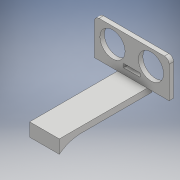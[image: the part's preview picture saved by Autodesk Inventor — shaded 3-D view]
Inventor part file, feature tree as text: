
AUTODESK INVENTOR PART (.ipt)
format: ipt  version: 2018 (Build 220112000, 112)  size: 144,384 bytes
history: native  units: mm
features: reference x3, other x3, extrude x2, sketch x2, projected_geometry x1
ambient origin geometry x8: Origin, YZ Plane, XZ Plane, XY Plane, X Axis, Y Axis, Z Axis, Center Point
bodies: Solid1 (feature_tree)
feature tree (11):
  extrude  "Extrusion1"  Depth=20.0mm TaperAngle=0.0deg
  extrude  "Extrusion3"  Depth=4.0mm
  sketch  "Sketch1"  dims[d0=15.0mm d2=20.0mm d3=0.0mm]
  reference  "Reference1"
  reference  "Reference2"
  reference  "Reference3"
  sketch  "Sketch4"  dims[d8=20.0mm d9=4.0mm d10=3.0mm d11=0.0mm d12=4.0mm]
  projected_geometry  "Projected Loop1"
  other  "<userpath>\OneDrive\Documents\Inventor\TSA\2018\Animatronics\Tortoise\TurtleAssembly2.iam"
  other  "TurtleAssembly2.iam"
  other  "Face:1"
